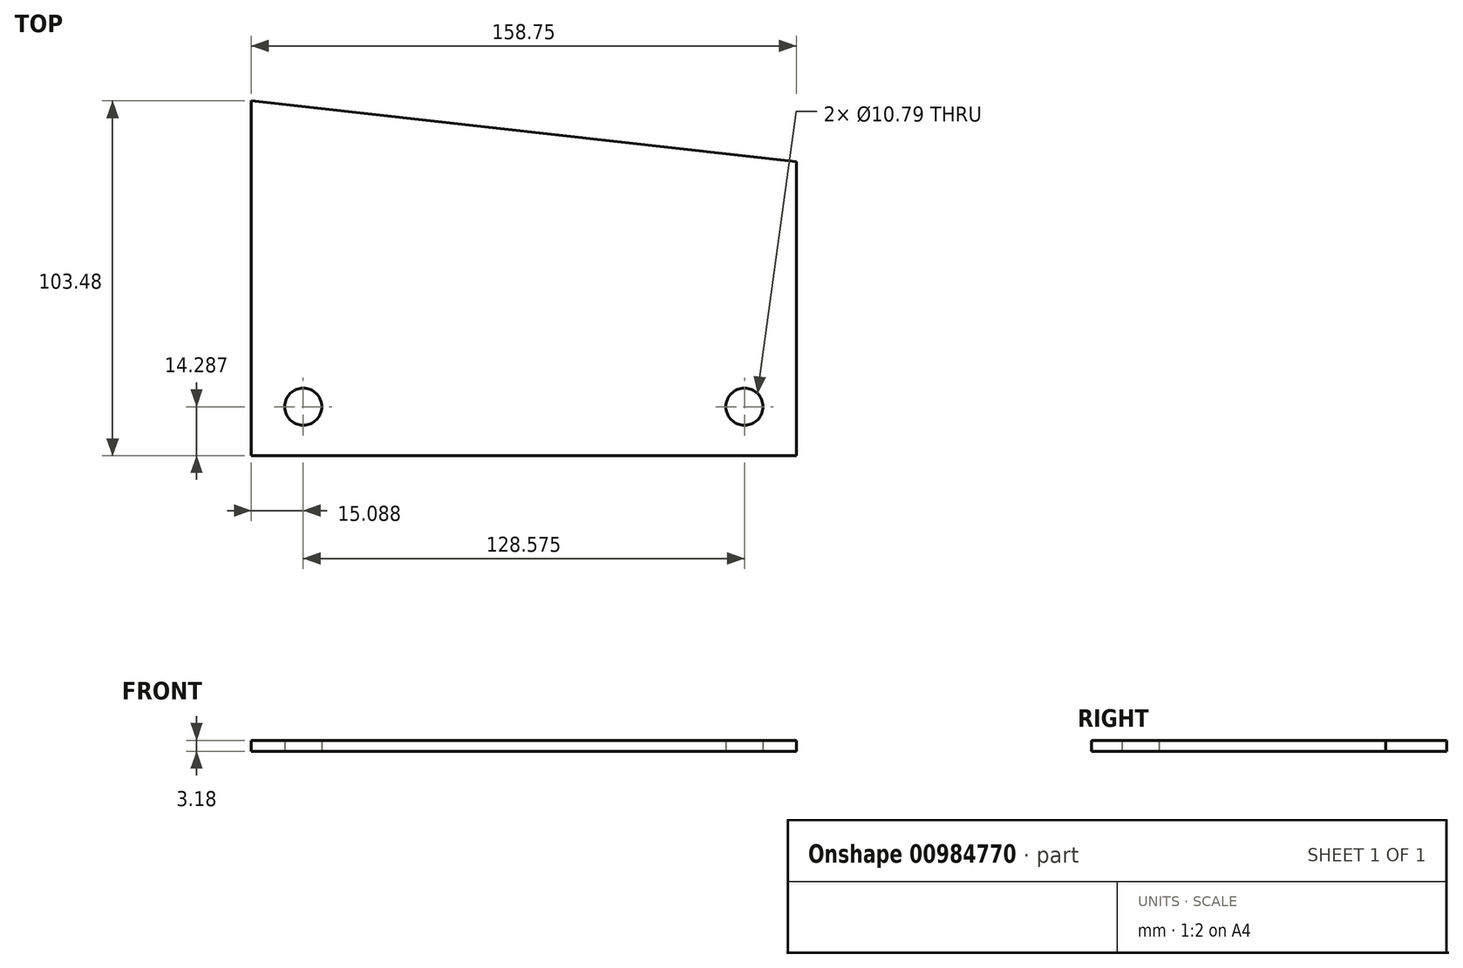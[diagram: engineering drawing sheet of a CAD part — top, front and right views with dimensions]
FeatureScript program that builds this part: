
annotation { "Feature Type Name" : "Feature", "Feature Type Description" : "" }
export const myFeature = defineFeature(function(context is Context, id is Id, definition is map)
    precondition{}
    {
        {
            var Q0;
            Q0=qCreatedBy(makeId("Top.planeOp"),FACE);
            var sketch = newSketch(context, id + "F0", { "sketchPlane" : qUnion([Q0])});
            skLineSegment(sketch, "E0.bottom", {"start": v(0, 0) * mm, "end": v(158.75, 0) * mm});
            skLineSegment(sketch, "E0.top", {"start": v(0, 65.07) * mm, "end": v(158.75, 65.07) * mm});
            skLineSegment(sketch, "E0.left", {"start": v(0, 0) * mm, "end": v(0, 65.07) * mm});
            skLineSegment(sketch, "E0.right", {"start": v(158.75, 0) * mm, "end": v(158.75, 65.07) * mm});
            skLineSegment(sketch, "E1", {"start": v(0, 65.07) * mm, "end": v(0, 103.48) * mm});
            skLineSegment(sketch, "E2", {"start": v(0, 103.48) * mm, "end": v(158.75, 85.7) * mm});
            skLineSegment(sketch, "E3", {"start": v(158.75, 85.7) * mm, "end": v(158.75, 65.07) * mm});
            skCircle(sketch, "E4", {"center": v(15.09, 14.29) * mm, "radius": 5.4 * mm});
            skCircle(sketch, "E5", {"center": v(143.66, 14.29) * mm, "radius": 5.4 * mm});
            skSolve(sketch);
        }
        {
            var Q0;
            Q0=makeQuery(id+"F0.imprint","IMPRINT",FACE,{"disambiguationData":[TD([[makeQuery(id+"F0.imprint","IMPRINT",EDGE,{"derivedFrom":sQuery(id+"F0.wireOp",EDGE,"E0.bottom")}),1.0]])]});
            var Q1;
            Q1=makeQuery(id+"F0.imprint","IMPRINT",FACE,{"disambiguationData":[TD([[makeQuery(id+"F0.imprint","IMPRINT",EDGE,{"derivedFrom":sQuery(id+"F0.wireOp",EDGE,"E0.top")}),1.0]])]});
            extrude(context, id + "F1", {"entities" : qUnion([Q0, Q1]), "depth" : 3.17 * mm, "offsetDistance" : 25.4 * mm});
        }
    });
